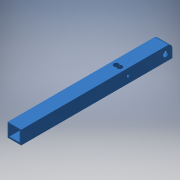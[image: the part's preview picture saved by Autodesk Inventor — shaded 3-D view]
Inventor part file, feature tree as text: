
AUTODESK INVENTOR PART (.ipt)
format: ipt  version: 2017 SP1 (Build 210196100, 196)  size: 139,264 bytes
history: native  units: in
note: dims shown in document units (in); Inventor stores cm internally (conversion verified against a paired STEP export)
features: extrude x3, sketch x3, fillet x1
ambient origin geometry x8: Origin, YZ Plane, XZ Plane, XY Plane, X Axis, Y Axis, Z Axis, Center Point
bodies: Solid1 (feature_tree)
feature tree (7):
  extrude  "Extrusion1"  Depth=0.125in
  extrude  "Extrusion2"  Depth=0.375in
  extrude  "Extrusion3"  Depth=0.125in TaperAngle=0.0deg
  fillet  "Fillet1"  Radius=0.375in
  sketch  "Sketch1"  dims[d0=1.0in d1=0.125in]
  sketch  "Sketch2"  dims[d2=11.125in d3=0.0in d4=0.375in]
  sketch  "Sketch3"  dims[d5=0.5in d6=5.5in d7=0.0in d8=0.375in d10=5.5in d11=0.0in d12=3.5in d13=0.375in d14=0.375in d15=0.125in d16=0.375in d19=0.2in d20=2.75in d21=0.125in]
